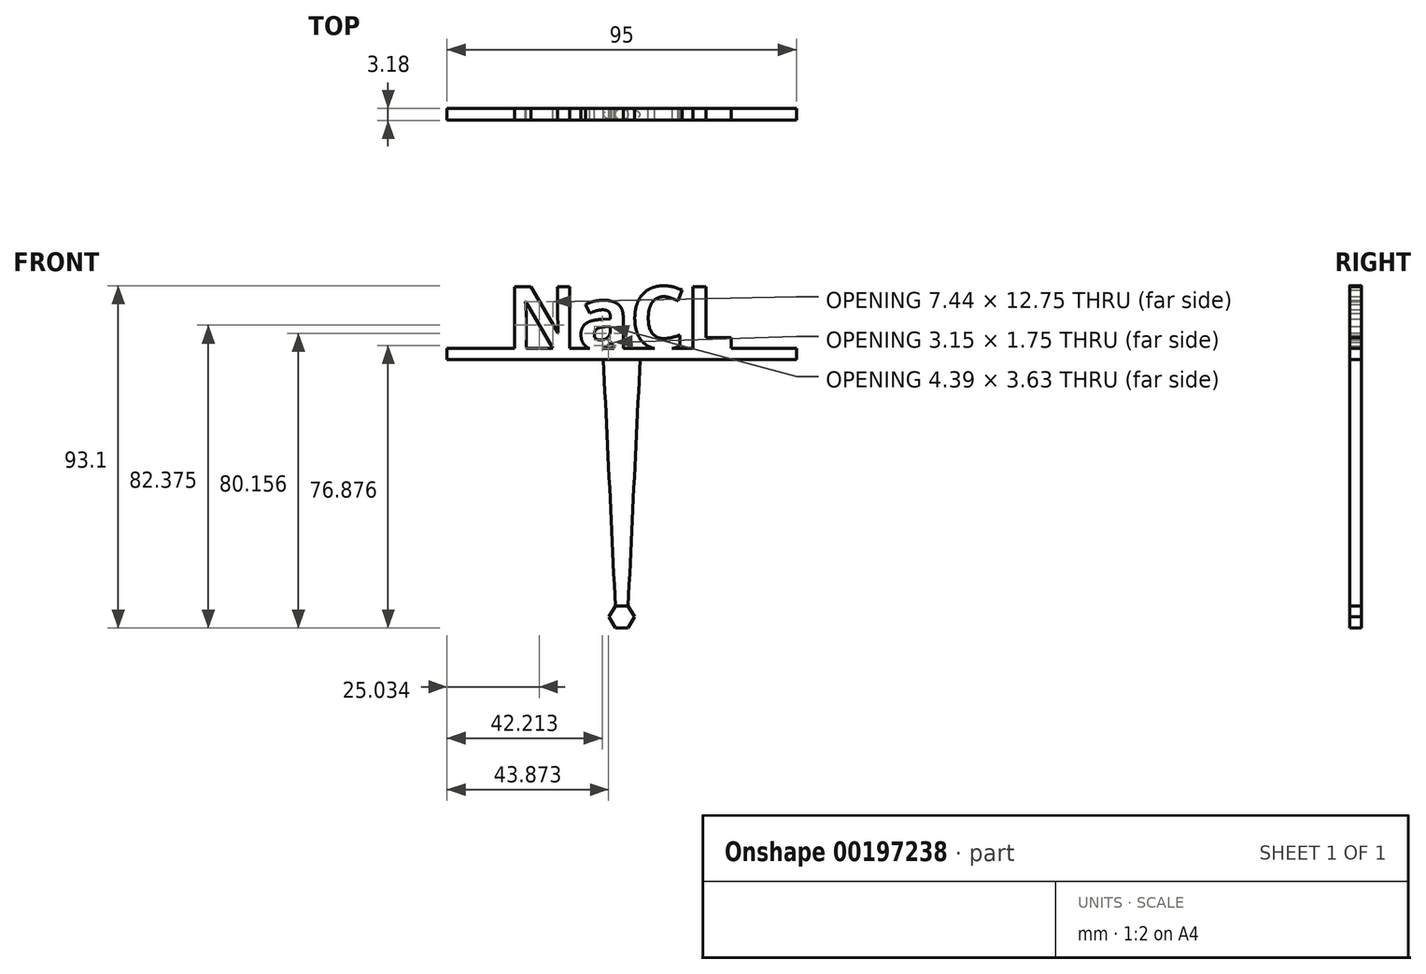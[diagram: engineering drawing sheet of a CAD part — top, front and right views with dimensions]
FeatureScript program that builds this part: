
annotation { "Feature Type Name" : "Feature", "Feature Type Description" : "" }
export const myFeature = defineFeature(function(context is Context, id is Id, definition is map)
    precondition{}
    {
        {
            var Q0;
            Q0=qCreatedBy(makeId("Front.planeOp"),FACE);
            var sketch = newSketch(context, id + "F0", { "sketchPlane" : qUnion([Q0])});
            skLineSegment(sketch, "E0.bottom", {"start": v(-47.5, 3) * mm, "end": v(47.5, 3) * mm});
            skLineSegment(sketch, "E0.top", {"start": v(-47.5, 0) * mm, "end": v(47.5, 0) * mm});
            skLineSegment(sketch, "E0.left", {"start": v(-47.5, 3) * mm, "end": v(-47.5, 0) * mm});
            skLineSegment(sketch, "E0.right", {"start": v(47.5, 3) * mm, "end": v(47.5, 0) * mm});
            skText(sketch, "E1", { "text": "NaCL\n", "fontName": "OpenSans-Bold.ttf"});
            const initialGuessF0  = {"E1": [-0.03128, 0.003, 1, 0, 0.017]};
            skSetInitialGuess(sketch, initialGuessF0);
            skSolve(sketch);
        }
        {
            var Q0;
            Q0=qSketchRegion(id+"F0",true);
            extrude(context, id + "F1", {"entities" : qUnion([Q0]), "depth" : 3.17 * mm});
        }
        {
            var Q0;
            Q0=qCreatedBy(makeId("Top.planeOp"),FACE);
            var sketch = newSketch(context, id + "F2", { "sketchPlane" : qUnion([Q0])});
            skLineSegment(sketch, "E2.bottom", {"start": v(0, 0) * mm, "end": v(2.5, 0) * mm, "construction": true});
            skLineSegment(sketch, "E2.top", {"start": v(0, -3.17) * mm, "end": v(2.5, -3.17) * mm, "construction": true});
            skLineSegment(sketch, "E2.left", {"start": v(0, 0) * mm, "end": v(0, -3.18) * mm, "construction": true});
            skLineSegment(sketch, "E2.right", {"start": v(2.5, 0) * mm, "end": v(2.5, -3.17) * mm, "construction": true});
            skEllipse(sketch, "E3", {"center": v(0, -1.59) * mm, "majorRadius": 5 * mm, "minorRadius": 1.59 * mm, "majorAxis": v(1, 0)});
            skSolve(sketch);
        }
        {
            var Q0;
            Q0=qCreatedBy(makeId("Top.planeOp"),FACE);
            cPlane(context, id + "F3", {"entities" : qUnion([Q0]), "cplaneType" : CPlaneType.OFFSET, "offset" : 70 * mm, "oppositeDirection" : true, "width" : 150 * mm, "height" : 150 * mm});
        }
        {
            var Q0;
            Q0=qCreatedBy(id+"F3.planeOp",FACE);
            var sketch = newSketch(context, id + "F4", { "sketchPlane" : qUnion([Q0])});
            skPoint(sketch, "E4", {"position": v(0, 0) * mm});
            skLineSegment(sketch, "E5.0", {"start": v(-50.9, -1.59) * mm, "end": v(49.1, -1.59) * mm, "construction": true});
            skLineSegment(sketch, "E6.0", {"start": v(0, 0) * mm, "end": v(0, -3.17) * mm, "construction": true});
            skCircle(sketch, "E7", {"center": v(0, -1.59) * mm, "radius": 1.59 * mm});
            skSolve(sketch);
        }
        {
            var Q1;
            Q1=makeQuery(id+"F2.imprint","IMPRINT",FACE,{"disambiguationData":[TD([[makeQuery(id+"F2.imprint","IMPRINT",EDGE,{"derivedFrom":sQuery(id+"F2.wireOp",EDGE,"E3")}),1.0]])]});
            var Q2;
            Q2=makeQuery(id+"F4.imprint","IMPRINT",FACE,{"disambiguationData":[TD([[makeQuery(id+"F4.imprint","IMPRINT",EDGE,{"derivedFrom":sQuery(id+"F4.wireOp",EDGE,"E7")}),1.0]])]});
            loft(context, id + "F5", {"operationType" : NewBodyOperationType.ADD, "sheetProfilesArray" : [{ "sheetProfileEntities" : qUnion([Q1]) }, { "sheetProfileEntities" : qUnion([Q2]) }]});
        }
        {
            var Q0;
            Q0=qCreatedBy(makeId("Front.planeOp"),FACE);
            var sketch = newSketch(context, id + "F6", { "sketchPlane" : qUnion([Q0])});
            skLineSegment(sketch, "E8.bottom", {"start": v(3, -73) * mm, "end": v(-3, -73) * mm, "construction": true});
            skLineSegment(sketch, "E8.top", {"start": v(3, -67) * mm, "end": v(-3, -67) * mm, "construction": true});
            skLineSegment(sketch, "E8.left", {"start": v(3, -73) * mm, "end": v(3, -67) * mm, "construction": true});
            skLineSegment(sketch, "E8.right", {"start": v(-3, -73) * mm, "end": v(-3, -67) * mm, "construction": true});
            skPoint(sketch, "E8.middle", {"position": v(0, -70) * mm});
            skCircle(sketch, "E9.cCircle", {"center": v(0, -70) * mm, "radius": 3 * mm, "construction": true});
            skLineSegment(sketch, "E9.0", {"start": v(0, -73) * mm, "end": v(-2.6, -71.5) * mm, "construction": true});
            skLineSegment(sketch, "E9.1", {"start": v(-2.6, -71.5) * mm, "end": v(-2.6, -68.5) * mm, "construction": true});
            skLineSegment(sketch, "E9.2", {"start": v(-2.6, -68.5) * mm, "end": v(0, -67) * mm, "construction": true});
            skLineSegment(sketch, "E9.3", {"start": v(0, -67) * mm, "end": v(2.6, -68.5) * mm, "construction": true});
            skLineSegment(sketch, "E9.4", {"start": v(2.6, -68.5) * mm, "end": v(2.6, -71.5) * mm, "construction": true});
            skLineSegment(sketch, "E9.5", {"start": v(2.6, -71.5) * mm, "end": v(0, -73) * mm, "construction": true});
            skLineSegment(sketch, "E10.0", {"start": v(1.73, -73) * mm, "end": v(-1.73, -73) * mm});
            skLineSegment(sketch, "E10.1", {"start": v(-1.73, -73) * mm, "end": v(-3.46, -70) * mm});
            skLineSegment(sketch, "E10.2", {"start": v(-3.46, -70) * mm, "end": v(-1.73, -67) * mm});
            skLineSegment(sketch, "E10.3", {"start": v(-1.73, -67) * mm, "end": v(1.73, -67) * mm});
            skLineSegment(sketch, "E10.4", {"start": v(1.73, -67) * mm, "end": v(3.46, -70) * mm});
            skLineSegment(sketch, "E10.5", {"start": v(3.46, -70) * mm, "end": v(1.73, -73) * mm});
            skPoint(sketch, "E10.0.midPoint", {"position": v(0, -73) * mm});
            skSolve(sketch);
        }
        {
            var Q0;
            Q0=makeQuery(id+"F6.imprint","IMPRINT",FACE,{"disambiguationData":[TD([[makeQuery(id+"F6.imprint","IMPRINT",EDGE,{"derivedFrom":sQuery(id+"F6.wireOp",EDGE,"E10.0")}),-1.0]])]});
            extrude(context, id + "F7", {"entities" : qUnion([Q0]), "operationType" : NewBodyOperationType.ADD, "depth" : 3.17 * mm});
        }
    });
